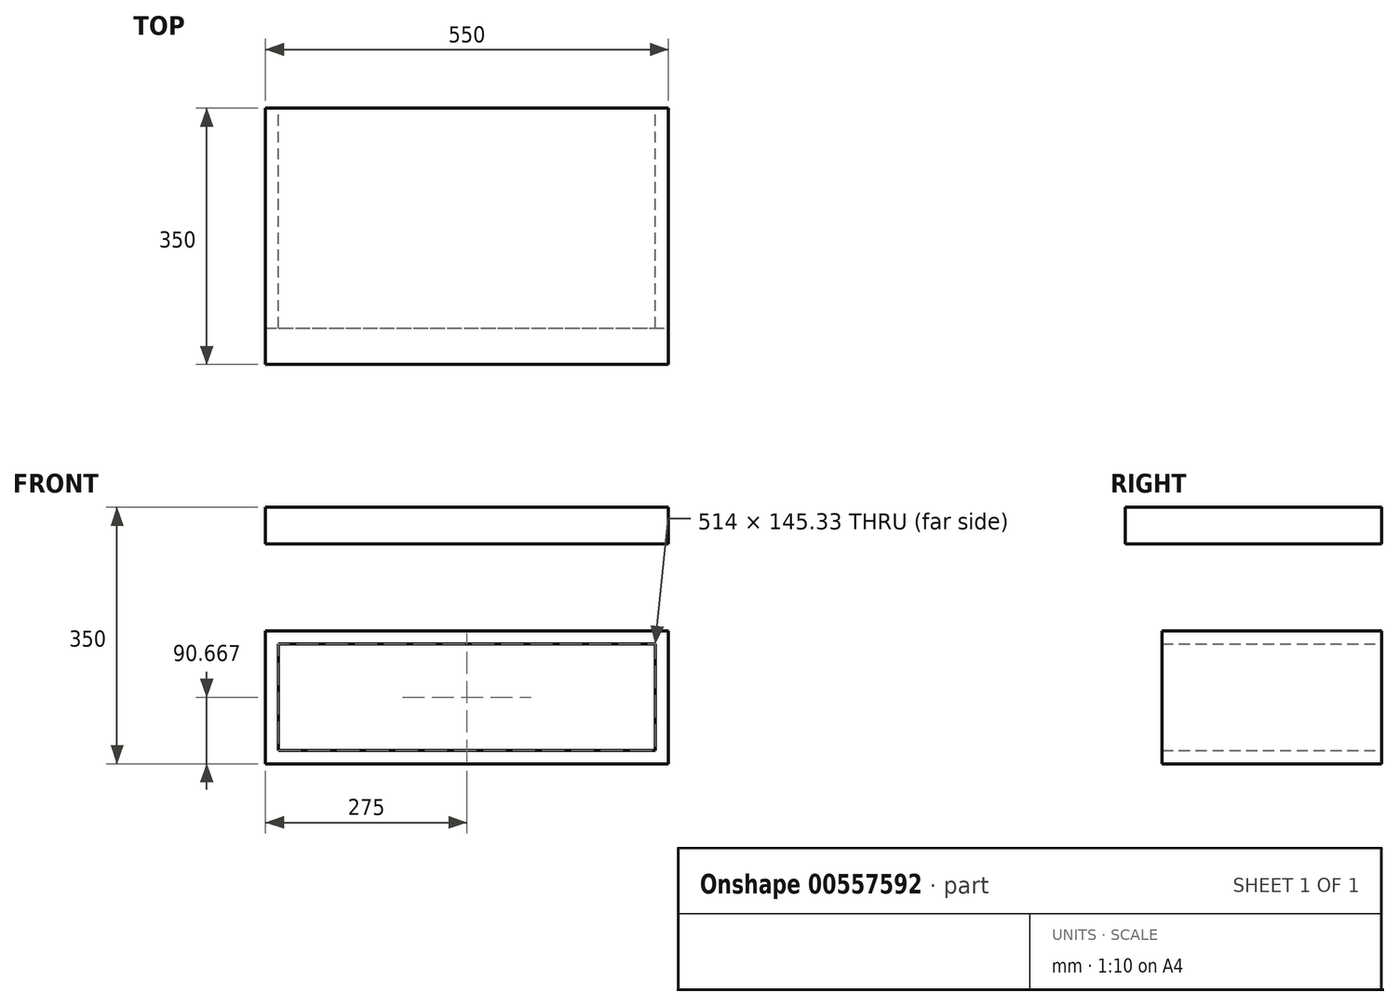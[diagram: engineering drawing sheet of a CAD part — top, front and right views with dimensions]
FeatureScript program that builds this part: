
annotation { "Feature Type Name" : "Feature", "Feature Type Description" : "" }
export const myFeature = defineFeature(function(context is Context, id is Id, definition is map)
    precondition{}
    {
        {
            var Q0;
            Q0=qCreatedBy(makeId("Top.planeOp"),FACE);
            var sketch = newSketch(context, id + "F0", { "sketchPlane" : qUnion([Q0])});
            skLineSegment(sketch, "E0.bottom", {"start": v(-300, 0) * mm, "end": v(300, 0) * mm});
            skLineSegment(sketch, "E0.top", {"start": v(-300, 18) * mm, "end": v(300, 18) * mm});
            skLineSegment(sketch, "E0.left", {"start": v(-300, 0) * mm, "end": v(-300, 18) * mm});
            skLineSegment(sketch, "E0.right", {"start": v(300, 0) * mm, "end": v(300, 18) * mm});
            skSolve(sketch);
        }
        {
            var Q0;
            Q0 = qConstructionFilter(qBodyType(qCreatedBy(id + "F0" ,EDGE), BodyType.WIRE), ConstructionObject.NO);
            var Q1;
            Q1 = qConstructionFilter(qBodyType(qCreatedBy(id + "F2" ,EDGE), BodyType.WIRE), ConstructionObject.NO);
            extrude(context, id + "F1", {"bodyType" : ToolBodyType.SURFACE, "surfaceEntities" : qUnion([Q0, Q1]), "depth" : 550 * mm, "offsetDistance" : 25 * mm});
        }
        {
            var Q0;
            Q0=qCreatedBy(makeId("Front.planeOp"),FACE);
            var sketch = newSketch(context, id + "F2", { "sketchPlane" : qUnion([Q0])});
            skLineSegment(sketch, "E1.bottom", {"start": v(-300, 0) * mm, "end": v(300, 0) * mm});
            skLineSegment(sketch, "E1.top", {"start": v(-300, -16.58) * mm, "end": v(300, -16.58) * mm});
            skLineSegment(sketch, "E1.left", {"start": v(-300, 0) * mm, "end": v(-300, -16.58) * mm});
            skLineSegment(sketch, "E1.right", {"start": v(300, 0) * mm, "end": v(300, -16.58) * mm});
            skSolve(sketch);
        }
        {
            var Q0;
            Q0=makeQuery(id+"F2.imprint","IMPRINT",FACE,{"disambiguationData":[TD([[makeQuery(id+"F2.imprint","IMPRINT",EDGE,{"derivedFrom":sQuery(id+"F2.wireOp",EDGE,"E1.bottom")}),-1.0]])]});
            var Q1;
            Q1 = qConstructionFilter(qBodyType(qCreatedBy(id + "F2" ,EDGE), BodyType.WIRE), ConstructionObject.NO);
            extrude(context, id + "F3", {"entities" : qUnion([Q0]), "bodyType" : ToolBodyType.SURFACE, "surfaceEntities" : qUnion([Q1]), "depth" : 350 * mm, "offsetDistance" : 25 * mm});
        }
        {
            var Q0;
            Q0=makeQuery(id+"F1.opExtrude","SWEPT_FACE",FACE,{"disambiguationData":[OSD([sQuery(id+"F0.wireOp",EDGE,"E0.bottom")])]});
            var sketch = newSketch(context, id + "F4", { "sketchPlane" : qUnion([Q0])});
            skLineSegment(sketch, "E2.bottom", {"start": v(275, 350) * mm, "end": v(-275, 350) * mm});
            skLineSegment(sketch, "E2.top", {"start": v(275, 300) * mm, "end": v(-275, 300) * mm});
            skLineSegment(sketch, "E2.left", {"start": v(275, 350) * mm, "end": v(275, 300) * mm});
            skLineSegment(sketch, "E2.right", {"start": v(-275, 350) * mm, "end": v(-275, 300) * mm});
            skSolve(sketch);
        }
        {
            var Q0;
            Q0=makeQuery(id+"F4.imprint","IMPRINT",FACE,{"disambiguationData":[TD([[makeQuery(id+"F4.imprint","IMPRINT",EDGE,{"derivedFrom":sQuery(id+"F4.wireOp",EDGE,"E2.bottom")}),1.0]])]});
            extrude(context, id + "F5", {"entities" : qUnion([Q0]), "depth" : -350 * mm, "offsetDistance" : 25 * mm});
        }
        {
            var Q0;
            Q0=makeQuery(id+"F1.opExtrude","SWEPT_FACE",FACE,{"disambiguationData":[OSD([sQuery(id+"F0.wireOp",EDGE,"E0.bottom")])]});
            var sketch = newSketch(context, id + "F6", { "sketchPlane" : qUnion([Q0])});
            skLineSegment(sketch, "E3.bottom", {"start": v(275, 181.33) * mm, "end": v(-275, 181.33) * mm});
            skLineSegment(sketch, "E3.top", {"start": v(275, 0) * mm, "end": v(-275, 0) * mm});
            skLineSegment(sketch, "E3.left", {"start": v(275, 181.33) * mm, "end": v(275, 0) * mm});
            skLineSegment(sketch, "E3.right", {"start": v(-275, 181.33) * mm, "end": v(-275, 0) * mm});
            skLineSegment(sketch, "E4.bottom", {"start": v(257, 163.33) * mm, "end": v(-257, 163.33) * mm});
            skLineSegment(sketch, "E4.top", {"start": v(257, 18) * mm, "end": v(-257, 18) * mm});
            skLineSegment(sketch, "E4.left", {"start": v(257, 163.33) * mm, "end": v(257, 18) * mm});
            skLineSegment(sketch, "E4.right", {"start": v(-257, 163.33) * mm, "end": v(-257, 18) * mm});
            skSolve(sketch);
        }
        {
            var Q0;
            Q0=makeQuery(id+"F6.imprint","IMPRINT",FACE,{"disambiguationData":[TD([[makeQuery(id+"F6.imprint","IMPRINT",EDGE,{"derivedFrom":sQuery(id+"F6.wireOp",EDGE,"E3.bottom")}),1.0]])]});
            extrude(context, id + "F7", {"entities" : qUnion([Q0]), "oppositeDirection" : true, "depth" : 300 * mm, "offsetDistance" : 25 * mm});
        }
    });
